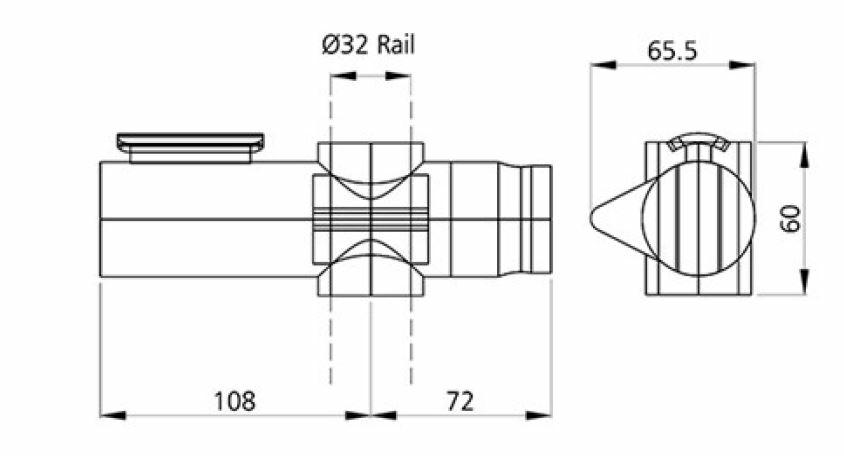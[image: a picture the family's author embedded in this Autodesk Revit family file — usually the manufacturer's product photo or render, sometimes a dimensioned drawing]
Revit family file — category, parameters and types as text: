
# Revit family: RBA4801-732
name_source: partatom
category: Plumbing Fixtures
units: mm (PartAtom-declared; Revit-internal decimal feet)

## family parameters
Always vertical = Yes
Cut with Voids When Loaded = No
Part Type = Normal
Room Calculation Point = No
Round Connector Dimension = Use Diameter
Shared = Yes
Work Plane-Based = No

## types (1)
- RBA4801-732
    CW Connection = Yes
    Default Elevation = 0 mm  [stored 0 ft]
    Description = Modular Shower Rail & Mixer Kit, Satin
    Distance Away from Toilet (default) = 1090 mm  [stored 3.57612 ft]
    Distance Away from Wall (default) = 100 mm  [stored 0.328084 ft]
    HW Connection = Yes
    Manufacturer = RBA Group
    Materials & Finishes = Stainless Steel Satin Finish
    Materials and Finishes = Stainless Steel Satin Finish
    Model = RBA4801-732
    OFFSET = 1000 mm  [stored 3.28084 ft]
    URL = www.rba.com.au
    Vent Connection = Yes
    Waste Connection = Yes

note: [stored X ft] marks values corroborated as IEEE doubles in the binary element streams (Revit-internal decimal feet)

## geometry (parser evidence)
native form markers: Blend x4, Sweep x13
no freeform markers — native parametric forms only
